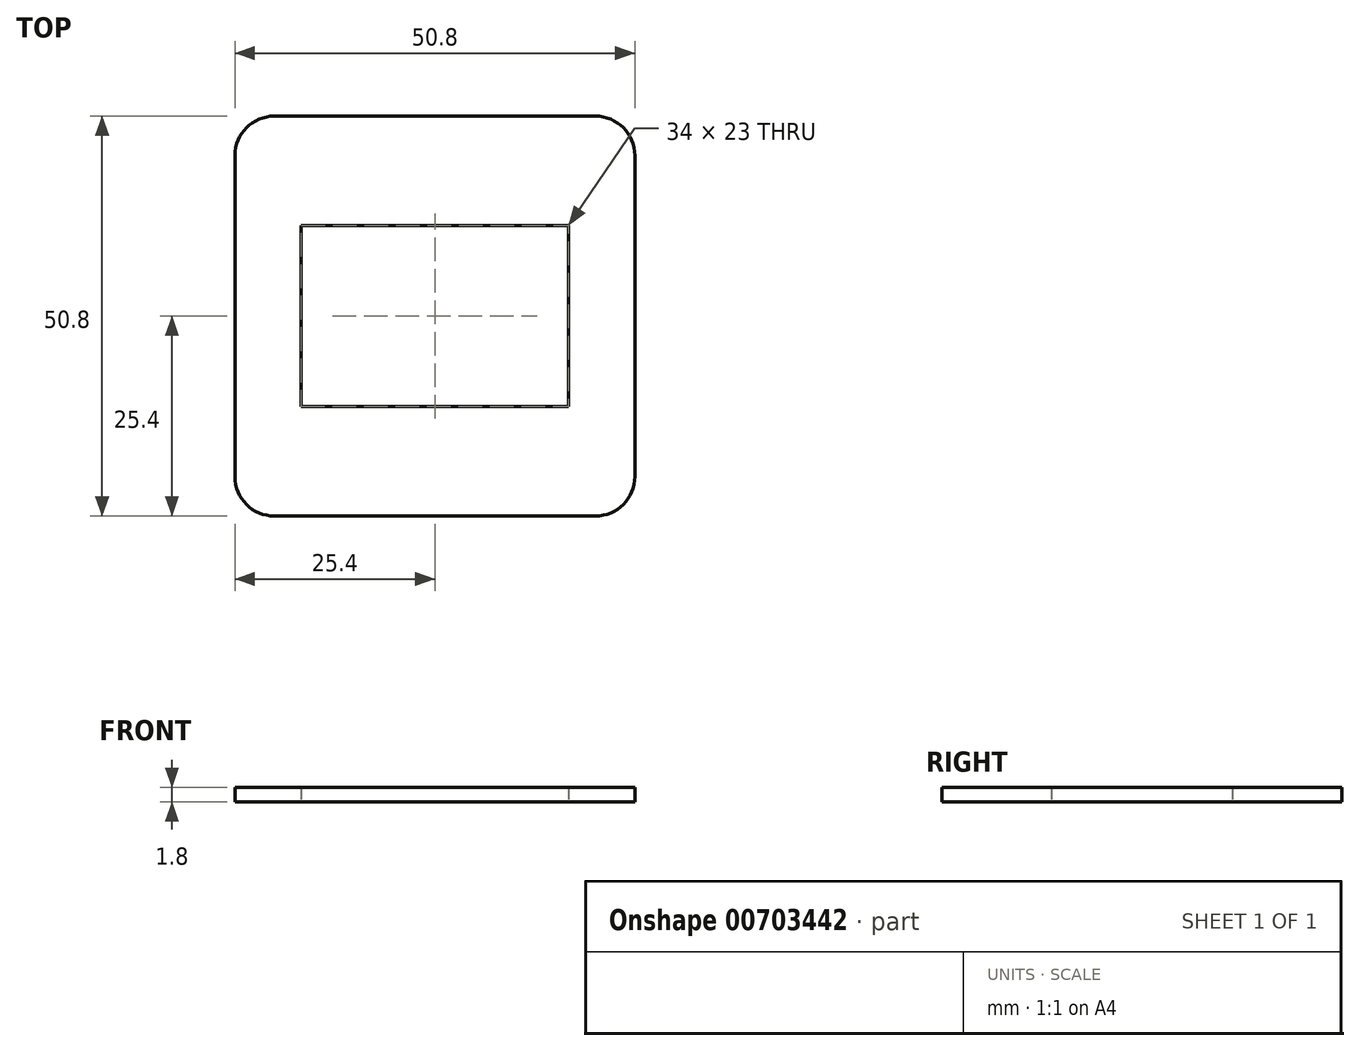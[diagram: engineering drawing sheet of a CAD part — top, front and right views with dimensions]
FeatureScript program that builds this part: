
annotation { "Feature Type Name" : "Feature", "Feature Type Description" : "" }
export const myFeature = defineFeature(function(context is Context, id is Id, definition is map)
    precondition{}
    {
        {
            var Q0;
            Q0=qCreatedBy(makeId("Top.planeOp"),FACE);
            var sketch = newSketch(context, id + "F0", { "sketchPlane" : qUnion([Q0])});
            skLineSegment(sketch, "E0.bottom", {"start": v(-20.4, 25.4) * mm, "end": v(20.4, 25.4) * mm});
            skLineSegment(sketch, "E0.top", {"start": v(-20.4, -25.4) * mm, "end": v(20.4, -25.4) * mm});
            skLineSegment(sketch, "E0.left", {"start": v(-25.4, 20.4) * mm, "end": v(-25.4, -20.4) * mm});
            skLineSegment(sketch, "E0.right", {"start": v(25.4, 20.4) * mm, "end": v(25.4, -20.4) * mm});
            skPoint(sketch, "E1.visualSharp", {"position": v(-25.4, 25.4) * mm});
            skArc(sketch, "E1.filletArc", {"start": v(-20.4, 25.4) * mm, "mid": v(-23.94, 23.94) * mm, "end": v(-25.4, 20.4) * mm});
            skPoint(sketch, "E2.visualSharp", {"position": v(25.4, 25.4) * mm});
            skArc(sketch, "E2.filletArc", {"start": v(25.4, 20.4) * mm, "mid": v(23.94, 23.94) * mm, "end": v(20.4, 25.4) * mm});
            skPoint(sketch, "E3.visualSharp", {"position": v(25.4, -25.4) * mm});
            skArc(sketch, "E3.filletArc", {"start": v(20.4, -25.4) * mm, "mid": v(23.94, -23.94) * mm, "end": v(25.4, -20.4) * mm});
            skPoint(sketch, "E4.visualSharp", {"position": v(-25.4, -25.4) * mm});
            skArc(sketch, "E4.filletArc", {"start": v(-25.4, -20.4) * mm, "mid": v(-23.94, -23.94) * mm, "end": v(-20.4, -25.4) * mm});
            skLineSegment(sketch, "E5.bottom", {"start": v(-17, 11.5) * mm, "end": v(17, 11.5) * mm});
            skLineSegment(sketch, "E5.top", {"start": v(-17, -11.5) * mm, "end": v(17, -11.5) * mm});
            skLineSegment(sketch, "E5.left", {"start": v(-17, 11.5) * mm, "end": v(-17, -11.5) * mm});
            skLineSegment(sketch, "E5.right", {"start": v(17, 11.5) * mm, "end": v(17, -11.5) * mm});
            skSolve(sketch);
        }
        {
            var Q0;
            Q0 = qSketchRegion(id + "F0", true);
            extrude(context, id + "F1", {"entities" : qUnion([Q0]), "depth" : 1.8 * mm, "offsetDistance" : 25 * mm});
        }
    });
